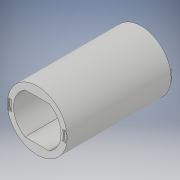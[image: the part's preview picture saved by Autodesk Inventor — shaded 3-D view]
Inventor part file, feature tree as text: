
AUTODESK INVENTOR PART (.ipt)
format: ipt  version: 2017 (Build 210142000, 142)  size: 145,408 bytes
history: native  units: in
note: dims shown in document units (in); Inventor stores cm internally (conversion verified against a paired STEP export)
features: extrude x3, sketch x3
ambient origin geometry x8: Origin, YZ Plane, XZ Plane, XY Plane, X Axis, Y Axis, Z Axis, Center Point
bodies: Solid1 (feature_tree)
feature tree (6):
  extrude  "corridor"  Depth=6.6667in
  extrude  "connection"  Depth=17.0in
  extrude  "receive"  Depth=0.25in
  sketch  "Sketch1"  dims[d0=6.6667in d1=4.0in]
  sketch  "Sketch3"  dims[d2=1.0in d3=17.0in d4=0.0in d7=1.0in]
  sketch  "Sketch4"  dims[d12=0.25in d13=0.0in d14=0.076in d15=0.076in d16=0.076in d17=0.076in d18=0.25in d19=0.0in]
